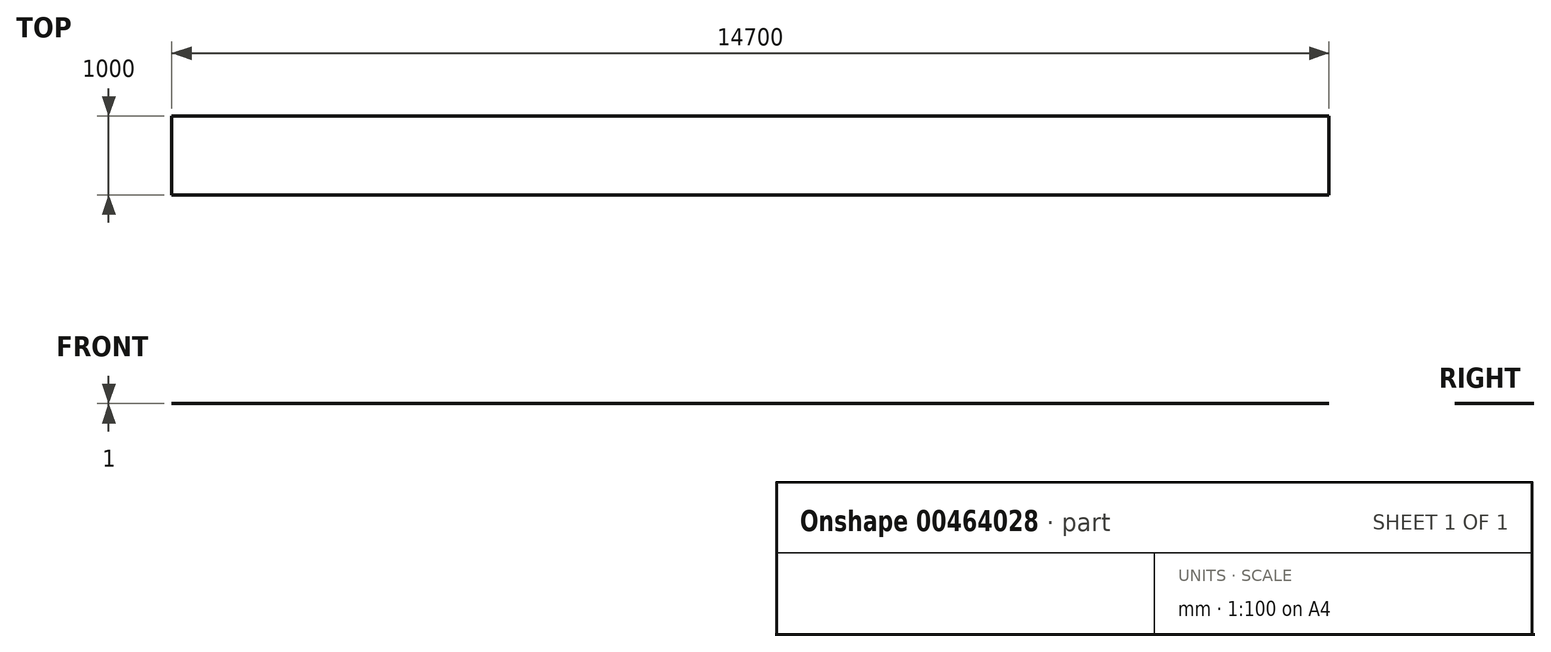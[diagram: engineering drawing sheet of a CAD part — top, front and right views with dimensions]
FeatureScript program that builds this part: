
annotation { "Feature Type Name" : "Feature", "Feature Type Description" : "" }
export const myFeature = defineFeature(function(context is Context, id is Id, definition is map)
    precondition{}
    {
        {
            var Q0;
            Q0=qCreatedBy(makeId("Top.planeOp"),FACE);
            var sketch = newSketch(context, id + "F0", { "sketchPlane" : qUnion([Q0])});
            skLineSegment(sketch, "E0.bottom", {"start": v(0, 0) * mm, "end": v(-14700, 0) * mm});
            skLineSegment(sketch, "E0.top", {"start": v(0, -1000) * mm, "end": v(-14700, -1000) * mm});
            skLineSegment(sketch, "E0.left", {"start": v(0, 0) * mm, "end": v(0, -1000) * mm});
            skLineSegment(sketch, "E0.right", {"start": v(-14700, 0) * mm, "end": v(-14700, -1000) * mm});
            skSolve(sketch);
        }
        {
            var Q0;
            Q0=qSketchRegion(id+"F0",true);
            extrude(context, id + "F1", {"entities" : qUnion([Q0]), "depth" : 1 * mm});
        }
    });
